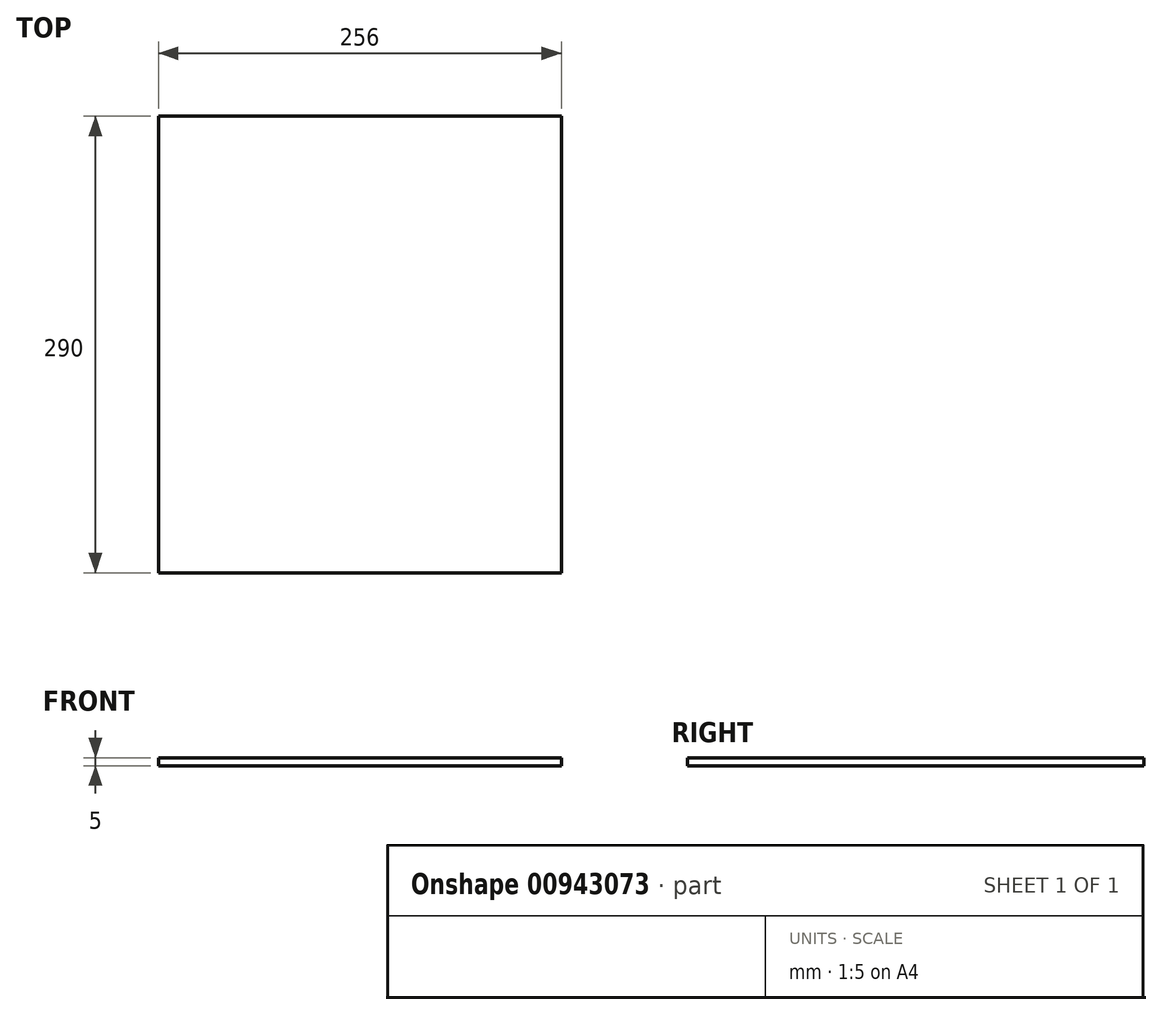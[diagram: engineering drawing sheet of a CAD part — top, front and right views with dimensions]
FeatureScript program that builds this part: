
annotation { "Feature Type Name" : "Feature", "Feature Type Description" : "" }
export const myFeature = defineFeature(function(context is Context, id is Id, definition is map)
    precondition{}
    {
        {
            var Q0;
            Q0=qCreatedBy(makeId("Top.planeOp"),FACE);
            var sketch = newSketch(context, id + "F0", { "sketchPlane" : qUnion([Q0])});
            skLineSegment(sketch, "E0.bottom", {"start": v(-133.33, 194.14) * mm, "end": v(122.67, 194.14) * mm});
            skLineSegment(sketch, "E0.top", {"start": v(-133.33, -95.86) * mm, "end": v(122.67, -95.86) * mm});
            skLineSegment(sketch, "E0.left", {"start": v(-133.33, 194.14) * mm, "end": v(-133.33, -95.86) * mm});
            skLineSegment(sketch, "E0.right", {"start": v(122.67, 194.14) * mm, "end": v(122.67, -95.86) * mm});
            skSolve(sketch);
        }
        {
            var Q0;
            Q0=makeQuery(id+"F0.imprint","IMPRINT",FACE,{"disambiguationData":[TD([[makeQuery(id+"F0.imprint","IMPRINT",EDGE,{"derivedFrom":sQuery(id+"F0.wireOp",EDGE,"E0.bottom")}),-1.0]])]});
            extrude(context, id + "F1", {"entities" : qUnion([Q0]), "depth" : 5 * mm, "offsetDistance" : 25 * mm});
        }
    });
